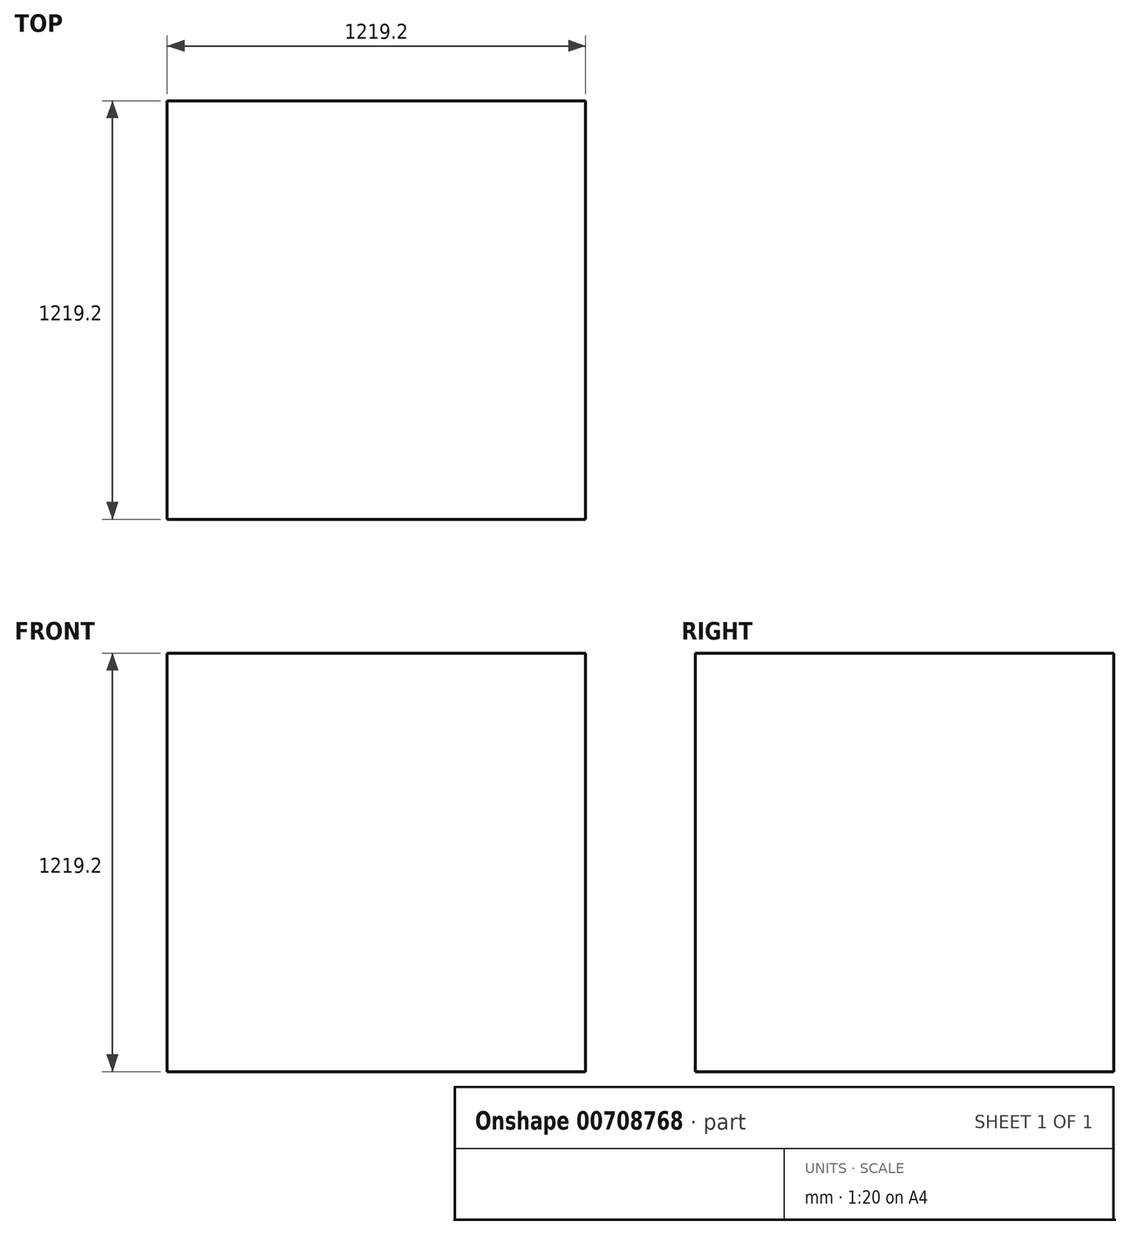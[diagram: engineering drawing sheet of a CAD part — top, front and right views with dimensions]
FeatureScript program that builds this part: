
annotation { "Feature Type Name" : "Feature", "Feature Type Description" : "" }
export const myFeature = defineFeature(function(context is Context, id is Id, definition is map)
    precondition{}
    {
        {
            var Q0;
            Q0=qCreatedBy(makeId("Front.planeOp"),FACE);
            var sketch = newSketch(context, id + "F0", { "sketchPlane" : qUnion([Q0])});
            skLineSegment(sketch, "E0.bottom", {"start": v(0, 0) * mm, "end": v(1219.2, 0) * mm});
            skLineSegment(sketch, "E0.top", {"start": v(0, 1219.2) * mm, "end": v(1219.2, 1219.2) * mm});
            skLineSegment(sketch, "E0.left", {"start": v(0, 0) * mm, "end": v(0, 1219.2) * mm});
            skLineSegment(sketch, "E0.right", {"start": v(1219.2, 0) * mm, "end": v(1219.2, 1219.2) * mm});
            skSolve(sketch);
        }
        {
            var Q0;
            Q0 = qSketchRegion(id + "F0", true);
            extrude(context, id + "F1", {"entities" : qUnion([Q0]), "depth" : 1219.2 * mm, "offsetDistance" : 25.4 * mm});
        }
    });
